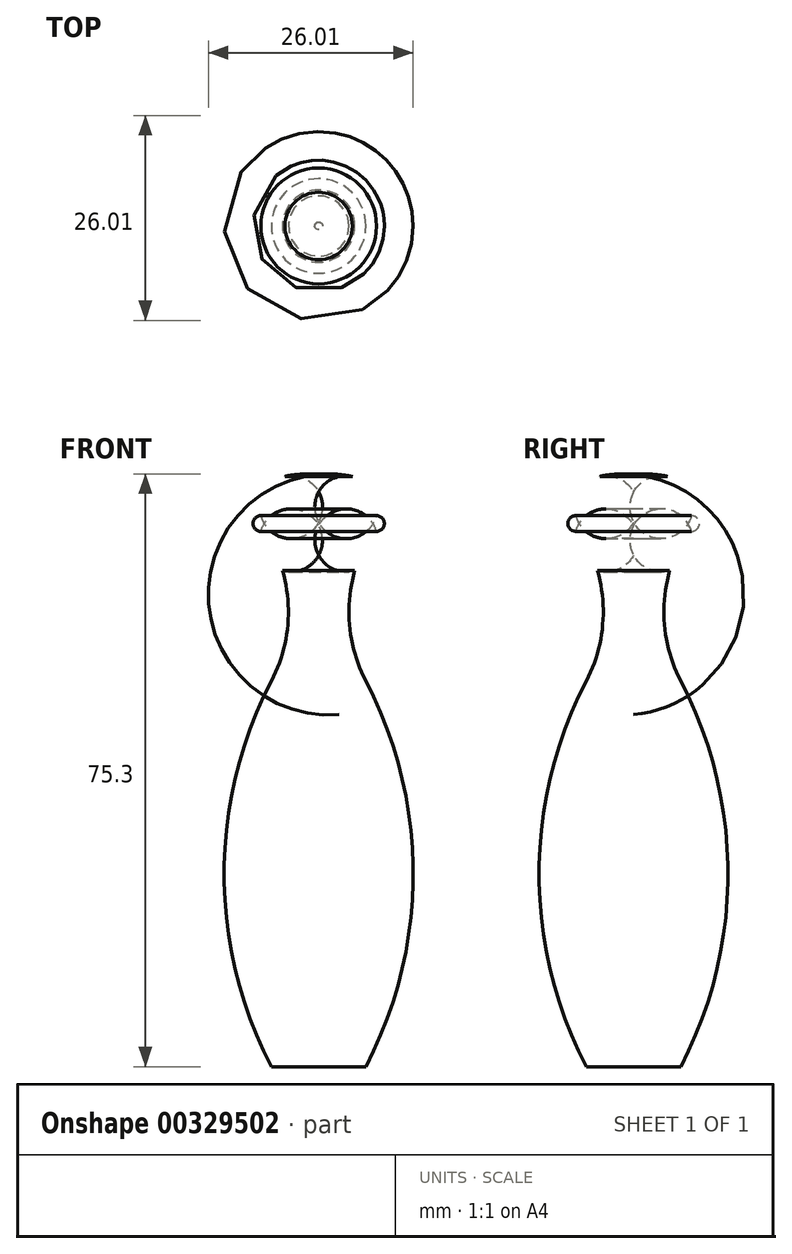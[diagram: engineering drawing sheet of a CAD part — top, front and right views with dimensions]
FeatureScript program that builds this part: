
annotation { "Feature Type Name" : "Feature", "Feature Type Description" : "" }
export const myFeature = defineFeature(function(context is Context, id is Id, definition is map)
    precondition{}
    {
        {
            var Q0;
            Q0=qCreatedBy(makeId("Front.planeOp"),FACE);
            var sketch = newSketch(context, id + "F0", { "sketchPlane" : qUnion([Q0])});
            skLineSegment(sketch, "E0", {"start": v(0, -75) * mm, "end": v(6, -75) * mm});
            skLineSegment(sketch, "E1", {"start": v(0, 0) * mm, "end": v(0, -75) * mm});
            skPoint(sketch, "E2.end.orphan", {"position": v(4.28, -0.88) * mm});
            skArc(sketch, "E3", {"start": v(6, -75) * mm, "mid": v(12, -50.5) * mm, "end": v(6, -26.01) * mm});
            skPoint(sketch, "E4.start.orphan", {"position": v(4.28, 2.91) * mm});
            skPoint(sketch, "E5.end.orphan", {"position": v(9.05, -0.88) * mm});
            skPoint(sketch, "E6.endSnap0", {"position": v(8.14, -10.21) * mm});
            skPoint(sketch, "E7.orphan", {"position": v(7.35, -8.16) * mm});
            skPoint(sketch, "E8.start.orphan", {"position": v(8.14, -9.58) * mm});
            skPoint(sketch, "E9.end.orphan", {"position": v(8.92, -12.26) * mm});
            skPoint(sketch, "E10.end.orphan", {"position": v(7.35, -14.02) * mm});
            skPoint(sketch, "E11.start.orphan", {"position": v(6, -8.38) * mm});
            skArc(sketch, "E12", {"start": v(4.58, -12) * mm, "mid": v(3.95, -19.14) * mm, "end": v(6, -26.01) * mm});
            skArc(sketch, "E13", {"start": v(4.58, -12) * mm, "mid": v(7.02, -10.08) * mm, "end": v(7.35, -7) * mm});
            skArc(sketch, "E14", {"start": v(7.35, -5) * mm, "mid": v(6.9, -1.83) * mm, "end": v(4.28, 0) * mm});
            skPoint(sketch, "E15.end.orphan", {"position": v(8.14, -7.56) * mm});
            skArc(sketch, "E16", {"start": v(7.35, -7) * mm, "mid": v(8.35, -6) * mm, "end": v(7.35, -5) * mm});
            skArc(sketch, "E17", {"start": v(4.28, 0) * mm, "mid": v(2.15, 0.27) * mm, "end": v(0, 0.24) * mm});
            skLineSegment(sketch, "E18", {"start": v(0, 0) * mm, "end": v(0, 0.24) * mm});
            skSolve(sketch);
        }
        {
            var Q0;
            Q0=makeQuery(id+"F0.imprint","IMPRINT",FACE,{"disambiguationData":[TD([[makeQuery(id+"F0.imprint","IMPRINT",EDGE,{"derivedFrom":sQuery(id+"F0.wireOp",EDGE,"E0")}),1.0]])]});
            var Q1;
            Q1=sQuery(id+"F0.wireOp",EDGE,"E1");
            revolve(context, id + "F1", {"entities" : qUnion([Q0]), "axis" : qUnion([Q1]), "revolveType" : RevolveType.FULL});
        }
    });
